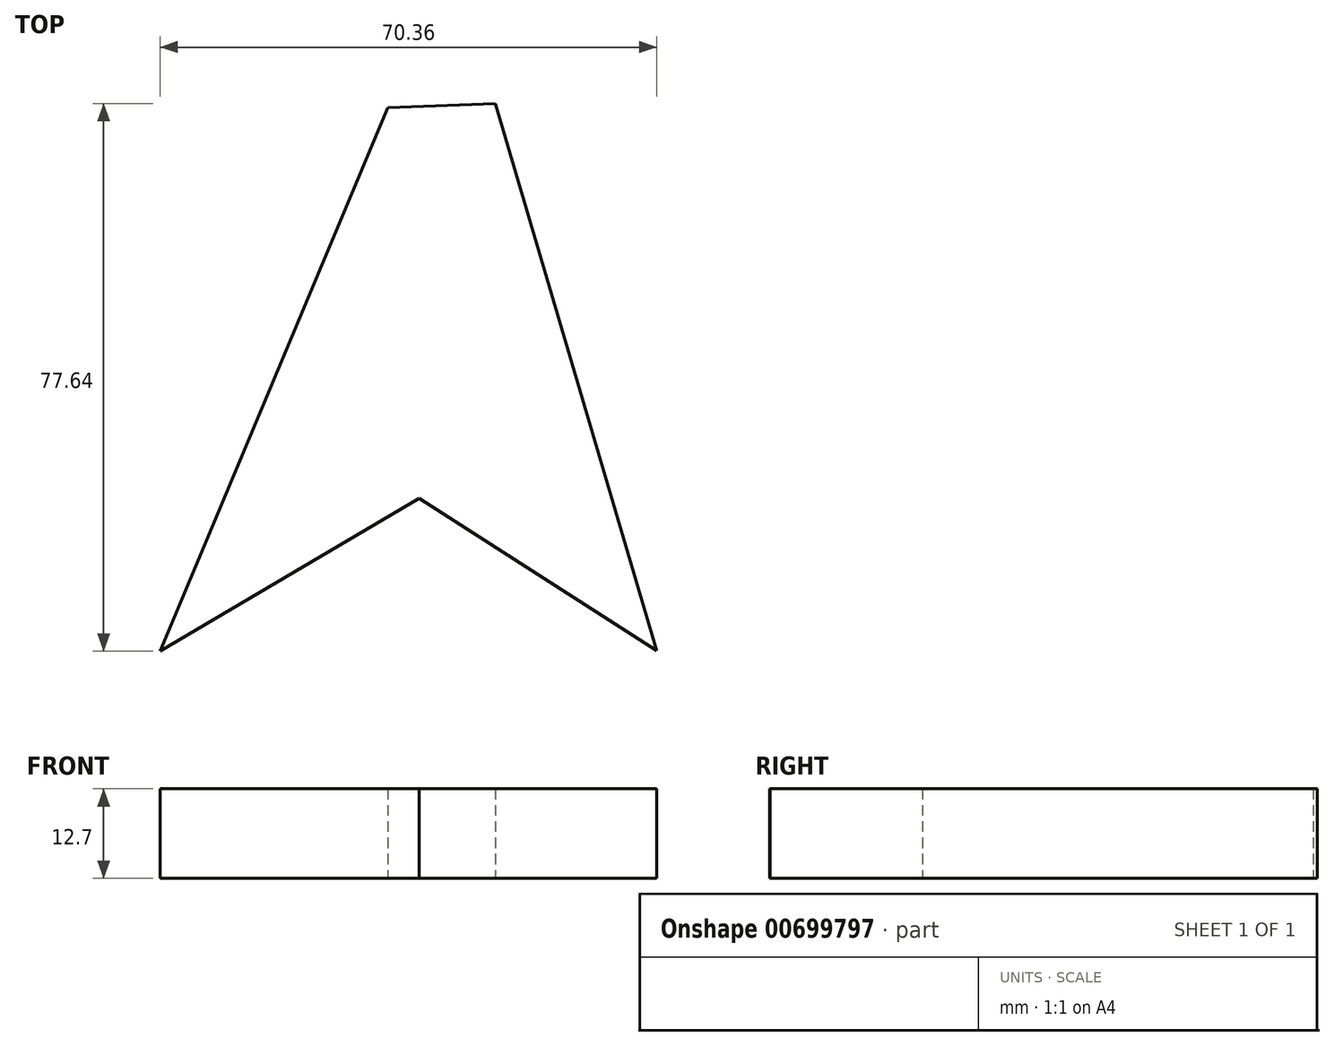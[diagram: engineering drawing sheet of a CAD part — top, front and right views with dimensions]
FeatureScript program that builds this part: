
annotation { "Feature Type Name" : "Feature", "Feature Type Description" : "" }
export const myFeature = defineFeature(function(context is Context, id is Id, definition is map)
    precondition{}
    {
        {
            var Q0;
            Q0=qCreatedBy(makeId("Top.planeOp"),FACE);
            var sketch = newSketch(context, id + "F0", { "sketchPlane" : qUnion([Q0])});
            skLineSegment(sketch, "E0", {"start": v(-43.74, 55.39) * mm, "end": v(-76, -21.65) * mm});
            skLineSegment(sketch, "E1", {"start": v(-76, -21.65) * mm, "end": v(-39.27, 0) * mm});
            skLineSegment(sketch, "E2", {"start": v(-39.27, 0) * mm, "end": v(-5.52, -21.65) * mm});
            skLineSegment(sketch, "E3", {"start": v(-5.52, -21.95) * mm, "end": v(-28.52, 55.99) * mm});
            skLineSegment(sketch, "E4", {"start": v(-28.52, 55.99) * mm, "end": v(-43.74, 55.39) * mm});
            skSolve(sketch);
        }
        {
            var Q0;
            Q0 = qSketchRegion(id + "F0", true);
            extrude(context, id + "F1", {"entities" : qUnion([Q0]), "depth" : 12.7 * mm, "offsetDistance" : 25.4 * mm});
        }
    });
